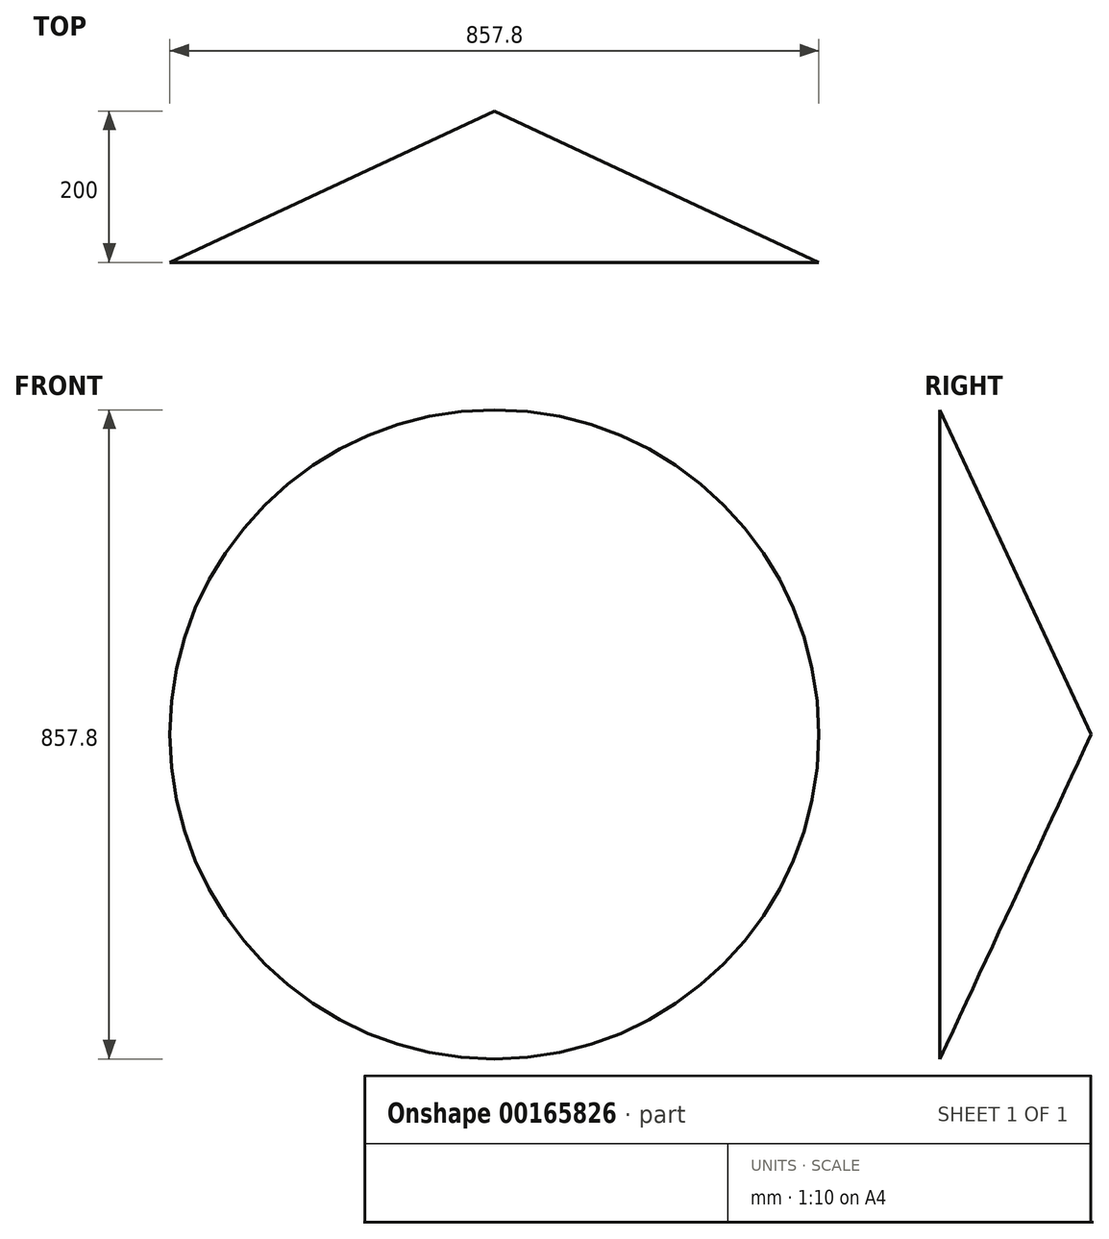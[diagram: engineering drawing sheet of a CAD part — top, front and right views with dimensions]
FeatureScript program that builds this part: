
annotation { "Feature Type Name" : "Feature", "Feature Type Description" : "" }
export const myFeature = defineFeature(function(context is Context, id is Id, definition is map)
    precondition{}
    {
        {
            var Q0;
            Q0=qCreatedBy(makeId("Right.planeOp"),FACE);
            var sketch = newSketch(context, id + "F0", { "sketchPlane" : qUnion([Q0])});
            skLineSegment(sketch, "E0", {"start": v(0, 0) * mm, "end": v(-200, 428.9) * mm});
            skLineSegment(sketch, "E1", {"start": v(-200, 428.9) * mm, "end": v(-200, 0) * mm});
            skLineSegment(sketch, "E2", {"start": v(-200, 0) * mm, "end": v(0, 0) * mm});
            skSolve(sketch);
        }
        {
            var Q0;
            Q0 = qSketchRegion(id + "F0", true);
            var Q1;
            Q1=sQuery(id+"F0.wireOp",EDGE,"E2");
            revolve(context, id + "F1", {"entities" : qUnion([Q0]), "axis" : qUnion([Q1]), "revolveType" : RevolveType.FULL});
        }
    });
